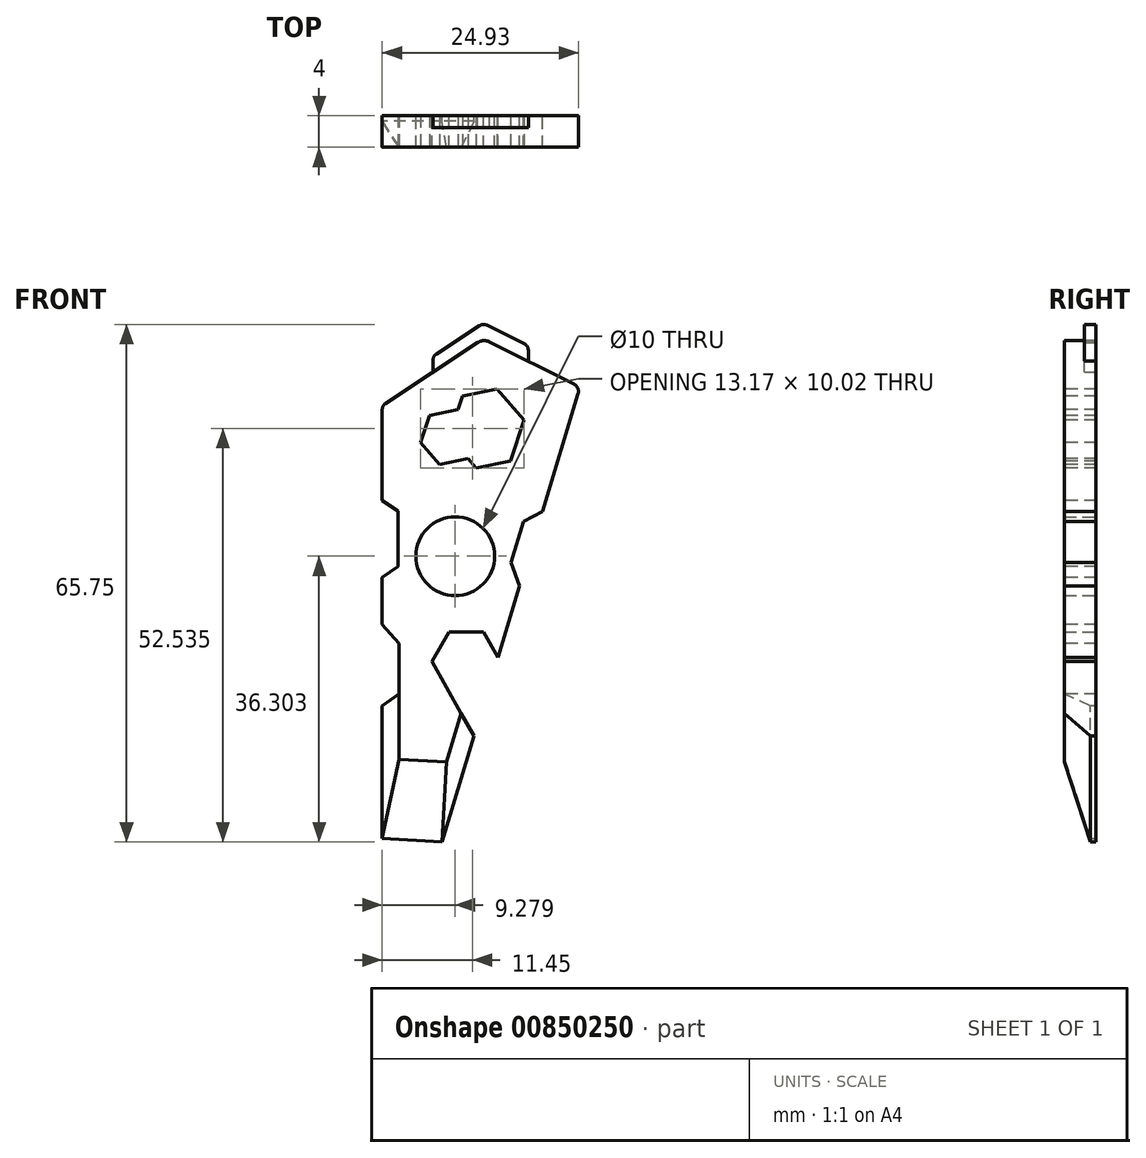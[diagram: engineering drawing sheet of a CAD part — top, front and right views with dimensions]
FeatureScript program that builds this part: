
annotation { "Feature Type Name" : "Feature", "Feature Type Description" : "" }
export const myFeature = defineFeature(function(context is Context, id is Id, definition is map)
    precondition{}
    {
        {
            var Q0;
            Q0=qCreatedBy(makeId("Front.planeOp"),FACE);
            var sketch = newSketch(context, id + "F0", { "sketchPlane" : qUnion([Q0])});
            skLineSegment(sketch, "E0", {"start": v(-11.47, 30.2) * mm, "end": v(-11.47, -24.8) * mm});
            skLineSegment(sketch, "E1", {"start": v(-11.47, 30.2) * mm, "end": v(1.39, 38.7) * mm});
            skLineSegment(sketch, "E2", {"start": v(1.39, 38.7) * mm, "end": v(13.66, 32.56) * mm});
            skLineSegment(sketch, "E3", {"start": v(13.66, 32.56) * mm, "end": v(-3.9, -25.23) * mm});
            skLineSegment(sketch, "E4", {"start": v(-3.9, -25.23) * mm, "end": v(-11.47, -24.8) * mm});
            skLineSegment(sketch, "E5", {"start": v(-11.47, 14.32) * mm, "end": v(-9.52, 12.95) * mm});
            skLineSegment(sketch, "E6", {"start": v(-9.52, 12.95) * mm, "end": v(-9.52, 5.97) * mm});
            skLineSegment(sketch, "E7", {"start": v(-9.52, 5.97) * mm, "end": v(-11.47, 4.6) * mm});
            skLineSegment(sketch, "E8", {"start": v(-11.47, -3.58) * mm, "end": v(-9.52, -4.94) * mm});
            skLineSegment(sketch, "E9", {"start": v(-9.52, -4.94) * mm, "end": v(-9.52, -11.42) * mm});
            skLineSegment(sketch, "E10", {"start": v(-9.52, -11.42) * mm, "end": v(-11.47, -12.78) * mm});
            skLineSegment(sketch, "E11", {"start": v(8.87, 16.78) * mm, "end": v(6.5, 15.51) * mm});
            skLineSegment(sketch, "E12", {"start": v(6.5, 15.51) * mm, "end": v(4.6, 9.28) * mm});
            skLineSegment(sketch, "E13", {"start": v(-5.04, 34.45) * mm, "end": v(-5.04, 36.45) * mm});
            skLineSegment(sketch, "E14", {"start": v(-5.04, 36.45) * mm, "end": v(1.36, 40.67) * mm});
            skLineSegment(sketch, "E15", {"start": v(1.36, 40.67) * mm, "end": v(7.88, 37.45) * mm});
            skLineSegment(sketch, "E16", {"start": v(7.88, 37.45) * mm, "end": v(7.1, 35.84) * mm});
            skLineSegment(sketch, "E17", {"start": v(7.1, 35.84) * mm, "end": v(7.1, 37.84) * mm});
            skLineSegment(sketch, "E18", {"start": v(5.98, 7.28) * mm, "end": v(4.91, 10.27) * mm});
            skCircle(sketch, "E19.cCircle", {"center": v(-0.8, -2.34) * mm, "radius": 3.79 * mm, "construction": true});
            skPoint(sketch, "E19.cCircle.perimeterSnap0", {"position": v(-10.5, -4.26) * mm});
            skLineSegment(sketch, "E19.0", {"start": v(3.58, -2.38) * mm, "end": v(1.37, -6.15) * mm});
            skLineSegment(sketch, "E19.1", {"start": v(1.37, -6.15) * mm, "end": v(-3, -6.11) * mm});
            skLineSegment(sketch, "E19.2", {"start": v(-3, -6.11) * mm, "end": v(-5.17, -2.3) * mm});
            skLineSegment(sketch, "E19.3", {"start": v(-5.17, -2.3) * mm, "end": v(-2.95, 1.46) * mm});
            skLineSegment(sketch, "E19.4", {"start": v(-2.95, 1.46) * mm, "end": v(1.42, 1.43) * mm});
            skLineSegment(sketch, "E19.5", {"start": v(1.42, 1.43) * mm, "end": v(3.58, -2.38) * mm});
            skPoint(sketch, "E19.0.midPoint", {"position": v(2.47, -4.26) * mm});
            skPoint(sketch, "E19.0.midPoint.positionSnap0", {"position": v(-10.5, -4.26) * mm});
            skLineSegment(sketch, "E20", {"start": v(-3, -6.11) * mm, "end": v(0.2, -11.76) * mm});
            skLineSegment(sketch, "E21", {"start": v(0.2, -11.76) * mm, "end": v(2.47, -4.26) * mm});
            skCircle(sketch, "E22", {"center": v(-2.2, 11.07) * mm, "radius": 5 * mm});
            skLineSegment(sketch, "E23", {"start": v(5.35, 11.72) * mm, "end": v(6.48, 8.93) * mm});
            skSolve(sketch);
        }
        {
            var Q0;
            {var subQ10=sQuery(id+"F0.wireOp",EDGE,"E1");Q0=makeQuery(id+"F0.imprint","IMPRINT",FACE,{"disambiguationData":[TD([[makeQuery(id+"F0.imprint","IMPRINT",EDGE,{"derivedFrom":subQ10}),-1.0]])]});}
            extrude(context, id + "F1", {"entities" : qUnion([Q0]), "depth" : 4 * mm, "offsetDistance" : 25 * mm});
        }
        {
            var Q0;
            Q0=makeQuery(id+"F1.opExtrude","CAP_FACE",FACE,{"disambiguationData":[OSD([sQuery(id+"F0.wireOp",EDGE,"E0"),sQuery(id+"F0.wireOp",EDGE,"E1"),sQuery(id+"F0.wireOp",EDGE,"E2"),sQuery(id+"F0.wireOp",EDGE,"E3"),sQuery(id+"F0.wireOp",EDGE,"E4"),sQuery(id+"F0.wireOp",EDGE,"E5"),sQuery(id+"F0.wireOp",EDGE,"E6"),sQuery(id+"F0.wireOp",EDGE,"E7"),sQuery(id+"F0.wireOp",EDGE,"E8"),sQuery(id+"F0.wireOp",EDGE,"E9"),sQuery(id+"F0.wireOp",EDGE,"E10"),sQuery(id+"F0.wireOp",EDGE,"E11"),sQuery(id+"F0.wireOp",EDGE,"E12"),sQuery(id+"F0.wireOp",EDGE,"lqKRGl02-UFkd-rBLG-R7Ko-Owrdx6a7nyhM"),sQuery(id+"F0.wireOp",EDGE,"ZaaIxhB7-tcXy-4Ahp-Yk5q-NKKAouVecxO1"),sQuery(id+"F0.wireOp",EDGE,"Luq659HK-MmLf-DaY7-koc5-HDhe4oF0Z7Sy"),sQuery(id+"F0.wireOp",EDGE,"I9mWue08-guui-Yc3Y-ypVq-9L99ieq9wwQ4"),sQuery(id+"F0.wireOp",EDGE,"o6OCr98v-eNuv-JsDV-KO2S-hzMIh74Hnolc"),sQuery(id+"F0.wireOp",EDGE,"IU5F9gLV-7Sm6-WQlf-WJ5t-pKr1KKp0RffR")])],"isStart":false});
            var sketch = newSketch(context, id + "F2", { "sketchPlane" : qUnion([Q0])});
            skCircle(sketch, "E24.cCircle", {"center": v(1.18, 27.3) * mm, "radius": 4.76 * mm, "construction": true});
            skLineSegment(sketch, "E24.0", {"start": v(6.56, 28.4) * mm, "end": v(4.83, 23.19) * mm});
            skLineSegment(sketch, "E24.1", {"start": v(4.83, 23.19) * mm, "end": v(-0.56, 22.09) * mm});
            skLineSegment(sketch, "E24.2", {"start": v(-0.56, 22.09) * mm, "end": v(-4.21, 26.2) * mm});
            skLineSegment(sketch, "E24.3", {"start": v(-4.21, 26.2) * mm, "end": v(-2.47, 31.42) * mm});
            skLineSegment(sketch, "E24.4", {"start": v(-2.47, 31.42) * mm, "end": v(2.92, 32.52) * mm});
            skLineSegment(sketch, "E24.5", {"start": v(2.92, 32.52) * mm, "end": v(6.56, 28.4) * mm});
            skPoint(sketch, "E24.0.midPoint", {"position": v(5.7, 25.8) * mm});
            skCircle(sketch, "E25.cCircle", {"center": v(-4.21, 26.2) * mm, "radius": 3.18 * mm, "construction": true});
            skLineSegment(sketch, "E25.0", {"start": v(-0.62, 26.93) * mm, "end": v(-1.78, 23.46) * mm});
            skLineSegment(sketch, "E25.1", {"start": v(-1.78, 23.46) * mm, "end": v(-5.37, 22.72) * mm});
            skLineSegment(sketch, "E25.2", {"start": v(-5.37, 22.72) * mm, "end": v(-7.8, 25.46) * mm});
            skLineSegment(sketch, "E25.3", {"start": v(-7.8, 25.46) * mm, "end": v(-6.64, 28.94) * mm});
            skLineSegment(sketch, "E25.4", {"start": v(-6.64, 28.94) * mm, "end": v(-3.05, 29.68) * mm});
            skLineSegment(sketch, "E25.5", {"start": v(-3.05, 29.68) * mm, "end": v(-0.62, 26.93) * mm});
            skPoint(sketch, "E25.0.midPoint", {"position": v(-1.2, 25.2) * mm});
            skCircle(sketch, "E26.cCircle", {"center": v(2.38, 27.31) * mm, "radius": 4.76 * mm, "construction": true});
            skLineSegment(sketch, "E26.0", {"start": v(7.77, 28.4) * mm, "end": v(6.02, 23.19) * mm});
            skLineSegment(sketch, "E26.1", {"start": v(6.02, 23.19) * mm, "end": v(0.63, 22.1) * mm});
            skLineSegment(sketch, "E26.2", {"start": v(0.63, 22.1) * mm, "end": v(-3.01, 26.22) * mm});
            skLineSegment(sketch, "E26.3", {"start": v(-3.01, 26.22) * mm, "end": v(-1.26, 31.43) * mm});
            skLineSegment(sketch, "E26.4", {"start": v(-1.26, 31.43) * mm, "end": v(4.13, 32.52) * mm});
            skLineSegment(sketch, "E26.5", {"start": v(4.13, 32.52) * mm, "end": v(7.77, 28.4) * mm});
            skPoint(sketch, "E26.0.midPoint", {"position": v(6.9, 25.8) * mm});
            skCircle(sketch, "E27.cCircle", {"center": v(-3.01, 26.22) * mm, "radius": 3.18 * mm, "construction": true});
            skLineSegment(sketch, "E27.0", {"start": v(0.58, 26.95) * mm, "end": v(-0.58, 23.47) * mm});
            skLineSegment(sketch, "E27.1", {"start": v(-0.58, 23.47) * mm, "end": v(-4.18, 22.74) * mm});
            skLineSegment(sketch, "E27.2", {"start": v(-4.18, 22.74) * mm, "end": v(-6.6, 25.5) * mm});
            skLineSegment(sketch, "E27.3", {"start": v(-6.6, 25.5) * mm, "end": v(-5.44, 28.97) * mm});
            skLineSegment(sketch, "E27.4", {"start": v(-5.44, 28.97) * mm, "end": v(-1.84, 29.7) * mm});
            skLineSegment(sketch, "E27.5", {"start": v(-1.84, 29.7) * mm, "end": v(0.58, 26.95) * mm});
            skPoint(sketch, "E27.0.midPoint", {"position": v(0, 25.2) * mm});
            skSolve(sketch);
        }
        {
            var Q0;
            Q0=makeQuery(id+"F1.opExtrude","SWEPT_EDGE",EDGE,{"disambiguationData":[OSD([sQuery(id+"F0.wireOp",EDGE,"E0"),sQuery(id+"F0.wireOp",EDGE,"E1")])]});
            var Q1;
            Q1=makeQuery(id+"F1.opExtrude","SWEPT_EDGE",EDGE,{"disambiguationData":[OSD([sQuery(id+"F0.wireOp",EDGE,"E2"),sQuery(id+"F0.wireOp",EDGE,"E3")])]});
            fillet(context, id + "F3", {"entities" : qUnion([Q0, Q1]), "radius" : 1 * mm, "tangentPropagation" : true, "allowEdgeOverflow" : false});
        }
        {
            var Q0;
            Q0=makeQuery(id+"F1.opExtrude","SWEPT_EDGE",EDGE,{"disambiguationData":[OSD([sQuery(id+"F0.wireOp",EDGE,"E1"),sQuery(id+"F0.wireOp",EDGE,"E2")])]});
            fillet(context, id + "F4", {"entities" : qUnion([Q0]), "radius" : 1.5 * mm, "tangentPropagation" : true, "allowEdgeOverflow" : false});
        }
        {
            var Q0;
            {var subQ1=sQuery(id+"F0.wireOp",EDGE,"E13");Q0=makeQuery(id+"F0.imprint","IMPRINT",FACE,{"disambiguationData":[TD([[makeQuery(id+"F0.imprint","IMPRINT",EDGE,{"derivedFrom":subQ1}),-1.0]])]});}
            extrude(context, id + "F5", {"entities" : qUnion([Q0]), "operationType" : NewBodyOperationType.ADD, "depth" : 1.5 * mm, "offsetDistance" : 25 * mm});
        }
        {
            var Q0;
            Q0=makeQuery(id+"F5.opExtrude","SWEPT_EDGE",EDGE,{"disambiguationData":[OSD([sQuery(id+"F0.wireOp",EDGE,"E1"),sQuery(id+"F0.wireOp",EDGE,"E2")])]});
            fillet(context, id + "F6", {"entities" : qUnion([Q0]), "radius" : 1.48 * mm, "tangentPropagation" : true, "allowEdgeOverflow" : false});
        }
        {
            var Q0;
            Q0=makeQuery(id+"F5.opExtrude","SWEPT_EDGE",EDGE,{"disambiguationData":[OSD([sQuery(id+"F0.wireOp",EDGE,"E14"),sQuery(id+"F0.wireOp",EDGE,"E15")])]});
            fillet(context, id + "F7", {"entities" : qUnion([Q0]), "radius" : 1 * mm, "tangentPropagation" : true, "allowEdgeOverflow" : false});
        }
        {
            var Q0;
            Q0=makeQuery(id+"F5.opExtrude","SWEPT_EDGE",EDGE,{"disambiguationData":[OSD([sQuery(id+"F0.wireOp",EDGE,"E15"),sQuery(id+"F0.wireOp",EDGE,"E17")])]});
            var Q1;
            Q1=makeQuery(id+"F5.opExtrude","SWEPT_EDGE",EDGE,{"disambiguationData":[OSD([sQuery(id+"F0.wireOp",EDGE,"E13"),sQuery(id+"F0.wireOp",EDGE,"E14")])]});
            fillet(context, id + "F8", {"entities" : qUnion([Q0, Q1]), "radius" : 1 * mm, "tangentPropagation" : true, "allowEdgeOverflow" : false});
        }
        {
            var Q0;
            {var subQ0=sQuery(id+"F0.wireOp",EDGE,"E5");Q0=makeQuery(id+"F0.imprint","IMPRINT",FACE,{"disambiguationData":[TD([[makeQuery(id+"F0.imprint","IMPRINT",EDGE,{"derivedFrom":subQ0}),-1.0]])]});}
            extrude(context, id + "F9", {"entities" : qUnion([Q0]), "operationType" : NewBodyOperationType.ADD, "depth" : 4 * mm, "offsetDistance" : 25 * mm});
        }
        {
            var Q0;
            {var subQ0=sQuery(id+"F0.wireOp",EDGE,"E8");Q0=makeQuery(id+"F0.imprint","IMPRINT",FACE,{"disambiguationData":[TD([[makeQuery(id+"F0.imprint","IMPRINT",EDGE,{"derivedFrom":subQ0}),-1.0]])]});}
            extrude(context, id + "F10", {"entities" : qUnion([Q0]), "operationType" : NewBodyOperationType.ADD, "depth" : 4 * mm, "offsetDistance" : 25 * mm});
        }
        {
            var Q0;
            {var subQ0=sQuery(id+"F0.wireOp",EDGE,"E10");var subQ1=sQuery(id+"F0.wireOp",EDGE,"E9");var subQ2=sQuery(id+"F0.wireOp",EDGE,"E8");var subQ3=sQuery(id+"F0.wireOp",EDGE,"E0");var subQ4=sQuery(id+"F0.wireOp",EDGE,"E7");var subQ5=sQuery(id+"F0.wireOp",EDGE,"E6");var subQ6=sQuery(id+"F0.wireOp",EDGE,"E5");Q0=makeQuery(id+"F10.boolean.opBoolean","MERGE",FACE,{"derivedFrom":[makeQuery(id+"F9.boolean.opBoolean","MERGE",FACE,{"derivedFrom":[makeQuery(id+"F1.opExtrude","CAP_FACE",FACE,{"disambiguationData":[OSD([subQ3,sQuery(id+"F0.wireOp",EDGE,"E1"),sQuery(id+"F0.wireOp",EDGE,"E2"),sQuery(id+"F0.wireOp",EDGE,"E3"),sQuery(id+"F0.wireOp",EDGE,"E4"),subQ6,subQ5,subQ4,subQ2,subQ1,subQ0,sQuery(id+"F0.wireOp",EDGE,"E11"),sQuery(id+"F0.wireOp",EDGE,"E12"),sQuery(id+"F0.wireOp",EDGE,"lqKRGl02-UFkd-rBLG-R7Ko-Owrdx6a7nyhM"),sQuery(id+"F0.wireOp",EDGE,"ZaaIxhB7-tcXy-4Ahp-Yk5q-NKKAouVecxO1"),sQuery(id+"F0.wireOp",EDGE,"Luq659HK-MmLf-DaY7-koc5-HDhe4oF0Z7Sy"),sQuery(id+"F0.wireOp",EDGE,"I9mWue08-guui-Yc3Y-ypVq-9L99ieq9wwQ4"),sQuery(id+"F0.wireOp",EDGE,"o6OCr98v-eNuv-JsDV-KO2S-hzMIh74Hnolc"),sQuery(id+"F0.wireOp",EDGE,"IU5F9gLV-7Sm6-WQlf-WJ5t-pKr1KKp0RffR")])],"isStart":false}),makeQuery(id+"F9.opExtrude","CAP_FACE",FACE,{"disambiguationData":[OSD([subQ3,subQ6,subQ5,subQ4])],"isStart":false})]}),makeQuery(id+"F10.opExtrude","CAP_FACE",FACE,{"disambiguationData":[OSD([subQ3,subQ2,subQ1,subQ0])],"isStart":false})]});}
            var sketch = newSketch(context, id + "F11", { "sketchPlane" : qUnion([Q0])});
            skLineSegment(sketch, "E28", {"start": v(-11.47, -7.94) * mm, "end": v(-9.31, -6.42) * mm});
            skLineSegment(sketch, "E29", {"start": v(-9.31, -6.42) * mm, "end": v(-9.31, 0) * mm});
            skLineSegment(sketch, "E30", {"start": v(-9.31, 0) * mm, "end": v(-11.47, 2.43) * mm});
            skLineSegment(sketch, "E31", {"start": v(-11.47, 8.4) * mm, "end": v(-9.48, 9.75) * mm});
            skLineSegment(sketch, "E32", {"start": v(-9.48, 9.75) * mm, "end": v(-9.48, 16.82) * mm});
            skLineSegment(sketch, "E33", {"start": v(-9.48, 16.82) * mm, "end": v(-11.47, 18.17) * mm});
            skArc(sketch, "E34", {"start": v(-11.47, -7.94) * mm, "mid": v(-9.36, -17.32) * mm, "end": v(-3.9, -25.23) * mm});
            skSolve(sketch);
        }
        {
            var Q0;
            {var subQ0=sQuery(id+"F11.wireOp",EDGE,"E31");Q0=makeQuery(id+"F11.imprint","IMPRINT",FACE,{"disambiguationData":[TD([[makeQuery(id+"F11.imprint","IMPRINT",EDGE,{"derivedFrom":subQ0}),1.0]])]});}
            extrude(context, id + "F12", {"entities" : qUnion([Q0]), "operationType" : NewBodyOperationType.REMOVE, "oppositeDirection" : true, "depth" : 25 * mm, "offsetDistance" : 25 * mm});
        }
        {
            var Q0;
            {var subQ0=sQuery(id+"F11.wireOp",EDGE,"E28");Q0=makeQuery(id+"F11.imprint","IMPRINT",FACE,{"disambiguationData":[TD([[makeQuery(id+"F11.imprint","IMPRINT",EDGE,{"derivedFrom":subQ0}),1.0]])]});}
            extrude(context, id + "F13", {"entities" : qUnion([Q0]), "operationType" : NewBodyOperationType.REMOVE, "oppositeDirection" : true, "depth" : 25 * mm, "offsetDistance" : 25 * mm});
        }
        {
            var Q0;
            {var subQ1=sQuery(id+"F2.wireOp",EDGE,"E24.0");Q0=makeQuery(id+"F2.imprint","IMPRINT",FACE,{"disambiguationData":[TD([[makeQuery(id+"F2.imprint","IMPRINT",EDGE,{"derivedFrom":subQ1}),-1.0]])]});}
            extrude(context, id + "F14", {"entities" : qUnion([Q0]), "operationType" : NewBodyOperationType.REMOVE, "oppositeDirection" : true, "depth" : 25 * mm, "offsetDistance" : 25 * mm});
        }
        {
            var Q0;
            {var subQ0=sQuery(id+"F2.wireOp",EDGE,"E27.3");Q0=makeQuery(id+"F2.imprint","IMPRINT",FACE,{"disambiguationData":[TD([[makeQuery(id+"F2.imprint","IMPRINT",EDGE,{"derivedFrom":subQ0}),-1.0]])]});}
            extrude(context, id + "F15", {"entities" : qUnion([Q0]), "operationType" : NewBodyOperationType.REMOVE, "oppositeDirection" : true, "depth" : 25 * mm, "offsetDistance" : 25 * mm});
        }
        {
            var Q0;
            {var subQ0=sQuery(id+"F2.wireOp",EDGE,"E25.5");var subQ1=sQuery(id+"F2.wireOp",EDGE,"E25.0");var subQ2=makeQuery(id+"F2.imprint","INTERSECT",VERTEX,{"derivedFrom":[subQ1,subQ0]});Q0=makeQuery(id+"F2.imprint","IMPRINT",FACE,{"disambiguationData":[TD([[makeQuery(id+"F2.imprint","IMPRINT",EDGE,{"disambiguationData":[TD([[subQ2,-1.0]])],"derivedFrom":subQ1}),-1.0]])]});}
            extrude(context, id + "F16", {"entities" : qUnion([Q0]), "operationType" : NewBodyOperationType.REMOVE, "oppositeDirection" : true, "depth" : 25 * mm, "offsetDistance" : 25 * mm});
        }
        {
            var Q0;
            {var subQ1=sQuery(id+"F2.wireOp",EDGE,"E24.2");var subQ5=sQuery(id+"F2.wireOp",EDGE,"E24.3");var subQ6=makeQuery(id+"F2.imprint","INTERSECT",VERTEX,{"derivedFrom":[subQ1,subQ5]});Q0=makeQuery(id+"F2.imprint","IMPRINT",FACE,{"disambiguationData":[TD([[makeQuery(id+"F2.imprint","IMPRINT",EDGE,{"disambiguationData":[TD([[subQ6,-1.0]])],"derivedFrom":subQ5}),-1.0]])]});}
            extrude(context, id + "F17", {"entities" : qUnion([Q0]), "operationType" : NewBodyOperationType.REMOVE, "oppositeDirection" : true, "depth" : 25 * mm, "offsetDistance" : 25 * mm});
        }
        {
            var Q0;
            {var subQ4=sQuery(id+"F2.wireOp",EDGE,"E27.0");Q0=makeQuery(id+"F2.imprint","IMPRINT",FACE,{"disambiguationData":[TD([[makeQuery(id+"F2.imprint","IMPRINT",EDGE,{"derivedFrom":subQ4}),-1.0]])]});}
            extrude(context, id + "F18", {"entities" : qUnion([Q0]), "operationType" : NewBodyOperationType.REMOVE, "oppositeDirection" : true, "depth" : 25 * mm, "offsetDistance" : 25 * mm});
        }
        {
            var Q0;
            {var subQ0=sQuery(id+"F2.wireOp",EDGE,"E27.4");var subQ1=sQuery(id+"F2.wireOp",EDGE,"E25.5");var subQ2=makeQuery(id+"F2.imprint","INTERSECT",VERTEX,{"derivedFrom":[subQ1,subQ0]});Q0=makeQuery(id+"F2.imprint","IMPRINT",FACE,{"disambiguationData":[TD([[makeQuery(id+"F2.imprint","IMPRINT",EDGE,{"disambiguationData":[TD([[subQ2,-1.0]])],"derivedFrom":subQ1}),1.0]])]});}
            extrude(context, id + "F19", {"entities" : qUnion([Q0]), "operationType" : NewBodyOperationType.REMOVE, "oppositeDirection" : true, "depth" : 25 * mm, "offsetDistance" : 25 * mm});
        }
        {
            var Q0;
            {var subQ1=sQuery(id+"F2.wireOp",EDGE,"E24.2");var subQ3=sQuery(id+"F2.wireOp",EDGE,"E27.1");var subQ4=makeQuery(id+"F2.imprint","INTERSECT",VERTEX,{"derivedFrom":[subQ1,subQ3]});Q0=makeQuery(id+"F2.imprint","IMPRINT",FACE,{"disambiguationData":[TD([[makeQuery(id+"F2.imprint","IMPRINT",EDGE,{"disambiguationData":[TD([[subQ4,-1.0]])],"derivedFrom":subQ1}),-1.0]])]});}
            extrude(context, id + "F20", {"entities" : qUnion([Q0]), "operationType" : NewBodyOperationType.REMOVE, "oppositeDirection" : true, "depth" : 25 * mm, "offsetDistance" : 25 * mm});
        }
        {
            var Q0;
            {var subQ3=sQuery(id+"F2.wireOp",EDGE,"E27.1");var subQ5=sQuery(id+"F2.wireOp",EDGE,"E27.2");var subQ7=makeQuery(id+"F2.imprint","INTERSECT",VERTEX,{"derivedFrom":[subQ3,subQ5]});Q0=makeQuery(id+"F2.imprint","IMPRINT",FACE,{"disambiguationData":[TD([[makeQuery(id+"F2.imprint","IMPRINT",EDGE,{"disambiguationData":[TD([[subQ7,1.0]])],"derivedFrom":subQ3}),-1.0]])]});}
            extrude(context, id + "F21", {"entities" : qUnion([Q0]), "operationType" : NewBodyOperationType.REMOVE, "oppositeDirection" : true, "depth" : 25 * mm, "offsetDistance" : 25 * mm});
        }
        {
            var Q0;
            {var subQ0=sQuery(id+"F0.wireOp",EDGE,"E4");var subQ1=sQuery(id+"F0.wireOp",EDGE,"E0");var subQ3=makeQuery(id+"F0.imprint","IMPRINT",EDGE,{"disambiguationData":[TD([[makeQuery(id+"F0.imprint","INTERSECT",VERTEX,{"derivedFrom":[subQ1,subQ0]}),1.0]])],"derivedFrom":subQ1});var subQ6=sQuery(id+"F0.wireOp",EDGE,"E7");var subQ8=makeQuery(id+"F0.imprint","IMPRINT",EDGE,{"disambiguationData":[TD([[makeQuery(id+"F0.imprint","INTERSECT",VERTEX,{"derivedFrom":[subQ1,subQ6]}),-1.0]])],"derivedFrom":subQ1});var subQ13=sQuery(id+"F0.wireOp",EDGE,"E1");var subQ15=makeQuery(id+"F0.imprint","IMPRINT",EDGE,{"disambiguationData":[TD([[makeQuery(id+"F0.imprint","INTERSECT",VERTEX,{"derivedFrom":[subQ1,subQ13]}),-1.0]])],"derivedFrom":subQ1});var subQ17=makeQuery(id+"F1.opExtrude","SWEPT_FACE",FACE,{"disambiguationData":[OSD([subQ0])]});Q0=makeQuery(id+"F13.boolean.opBoolean","SPLIT",EDGE,{"disambiguationData":[TD([subQ17])],"derivedFrom":makeQuery(id+"F12.boolean.opBoolean","SPLIT",EDGE,{"disambiguationData":[TD([subQ17])],"derivedFrom":makeQuery(id+"F10.boolean.opBoolean","MERGE",EDGE,{"derivedFrom":[makeQuery(id+"F1.opExtrude","CAP_EDGE",EDGE,{"disambiguationData":[OSD([subQ1]),TDD([subQ3])],"isStart":false}),makeQuery(id+"F9.boolean.opBoolean","MERGE",EDGE,{"derivedFrom":[makeQuery(id+"F1.opExtrude","CAP_EDGE",EDGE,{"disambiguationData":[OSD([subQ1]),TDD([subQ8])],"isStart":false}),makeQuery(id+"F1.opExtrude","CAP_EDGE",EDGE,{"disambiguationData":[OSD([subQ1]),TDD([subQ15])],"isStart":false}),makeQuery(id+"F9.opExtrude","CAP_EDGE",EDGE,{"disambiguationData":[OSD([subQ1])],"isStart":false})]}),makeQuery(id+"F10.opExtrude","CAP_EDGE",EDGE,{"disambiguationData":[OSD([subQ1])],"isStart":false})]})})});}
            chamfer(context, id + "F22", {"entities" : qUnion([Q0]), "chamferType" : ChamferType.OFFSET_ANGLE, "width" : 2.15 * mm, "oppositeDirection" : false, "angle" : 57 * degree, "tangentPropagation" : true});
        }
        {
            var Q0;
            {var subQ0=sQuery(id+"F0.wireOp",EDGE,"E3");Q0=makeQuery(id+"F1.opExtrude","CAP_EDGE",EDGE,{"disambiguationData":[OSD([subQ0]),TDD([makeQuery(id+"F0.imprint","IMPRINT",EDGE,{"disambiguationData":[TD([[makeQuery(id+"F0.imprint","INTERSECT",VERTEX,{"derivedFrom":[subQ0,sQuery(id+"F0.wireOp",EDGE,"E4")]}),1.0]])],"derivedFrom":subQ0})])],"isStart":false});}
            chamfer(context, id + "F23", {"entities" : qUnion([Q0]), "chamferType" : ChamferType.OFFSET_ANGLE, "width" : 3.3 * mm, "oppositeDirection" : false, "angle" : 36 * degree, "tangentPropagation" : true});
        }
        {
            var Q0;
            Q0=makeQuery(id+"F1.opExtrude","CAP_EDGE",EDGE,{"disambiguationData":[OSD([sQuery(id+"F0.wireOp",EDGE,"E4")])],"isStart":false});
            chamfer(context, id + "F24", {"entities" : qUnion([Q0]), "chamferType" : ChamferType.OFFSET_ANGLE, "width" : 3.3 * mm, "oppositeDirection" : false, "angle" : 72 * degree, "tangentPropagation" : true});
        }
    });
